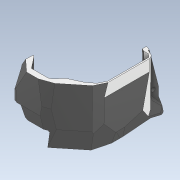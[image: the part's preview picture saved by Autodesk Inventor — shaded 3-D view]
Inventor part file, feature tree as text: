
AUTODESK INVENTOR PART (.ipt)
format: ipt  version: 2022.1 (Build 261234020, 234B)  size: 1,708,032 bytes
history: native  units: mm
features: delete_face x46, move_body x22, chamfer x20, direct_edit x18, sketch x9, projected_geometry x9, extrude x8, plane x4, hole x1, other x1
ambient origin geometry x8: Origin, YZ Plane, XZ Plane, XY Plane, X Axis, Y Axis, Z Axis, Center Point
bodies: Volumenkörper1 (feature_tree)
feature tree (138):
  extrude  "Extrusion1"  Depth=2.0mm TaperAngle=0.0deg
  delete_face  "Fläche löschen1"
  delete_face  "Fläche löschen2"
  delete_face  "Fläche löschen3"
  delete_face  "Fläche löschen4"
  direct_edit  "Direktbearbeitung1"
  plane  "Arbeitsebene2"
  extrude  "Extrusion2"  Depth=1.0mm TaperAngle=0.0deg
  delete_face  "Fläche löschen5"
  delete_face  "Fläche löschen6"
  delete_face  "Fläche löschen7"
  delete_face  "Fläche löschen8"
  delete_face  "Fläche löschen9"
  delete_face  "Fläche löschen10"
  direct_edit  "Direktbearbeitung2"
  delete_face  "Fläche löschen11"
  direct_edit  "Direktbearbeitung3"
  chamfer  "Fase1"  [1 undecoded]
  direct_edit  "Direktbearbeitung4"
  chamfer  "Fase2"  [1 undecoded]
  chamfer  "Fase3"  [1 undecoded]
  delete_face  "Fläche löschen12"
  direct_edit  "Direktbearbeitung5"
  direct_edit  "Direktbearbeitung6"
  direct_edit  "Direktbearbeitung7"
  direct_edit  "Direktbearbeitung8"
  extrude  "Extrusion3"  TaperAngle=0.0deg  [1 undecoded]
  chamfer  "Fase4"  [1 undecoded]
  delete_face  "Fläche löschen13"
  direct_edit  "Direktbearbeitung9"
  delete_face  "Fläche löschen14"
  direct_edit  "Direktbearbeitung10"
  chamfer  "Fase5"  Distance=1.0mm Angle=45.0deg
  direct_edit  "Direktbearbeitung11"
  delete_face  "Fläche löschen15"
  delete_face  "Fläche löschen16"
  chamfer  "Fase6"  Distance=1.598mm Angle=45.0deg
  extrude  "Extrusion4"  TaperAngle=0.0deg  [1 undecoded]
  chamfer  "Fase7"  [1 undecoded]
  delete_face  "Fläche löschen17"
  delete_face  "Fläche löschen18"
  delete_face  "Fläche löschen19"
  delete_face  "Fläche löschen20"
  delete_face  "Fläche löschen21"
  delete_face  "Fläche löschen22"
  delete_face  "Fläche löschen23"
  extrude  "Extrusion5"  Depth=10.0mm TaperAngle=0.0deg
  delete_face  "Fläche löschen24"
  chamfer  "Fase8"  Distance=0.2mm Angle=45.0deg
  delete_face  "Fläche löschen25"
  delete_face  "Fläche löschen26"
  plane  "Arbeitsebene3"
  extrude  "Extrusion6"  TaperAngle=0.0deg  [1 undecoded]
  delete_face  "Fläche löschen27"
  chamfer  "Fase9"  Distance=2.0mm Angle=45.0deg
  direct_edit  "Direktbearbeitung12"
  chamfer  "Fase10"  [1 undecoded]
  chamfer  "Fase11"  [1 undecoded]
  chamfer  "Fase12"  Distance=2.0mm Angle=45.0deg
  chamfer  "Fase13"  Distance=0.6mm
  delete_face  "Fläche löschen28"
  direct_edit  "Direktbearbeitung13"
  delete_face  "Fläche löschen29"
  delete_face  "Fläche löschen30"
  delete_face  "Fläche löschen31"
  delete_face  "Fläche löschen32"
  delete_face  "Fläche löschen33"
  delete_face  "Fläche löschen34"
  chamfer  "Fase14"  Distance=2.0mm Angle=45.0deg
  delete_face  "Fläche löschen35"
  delete_face  "Fläche löschen36"
  direct_edit  "Direktbearbeitung14"
  direct_edit  "Direktbearbeitung15"
  extrude  "Extrusion7"  Depth=1.0mm
  chamfer  "Fase15"  [1 undecoded]
  chamfer  "Fase16"  Distance=1.0mm
  chamfer  "Fase17"  [1 undecoded]
  delete_face  "Fläche löschen37"
  chamfer  "Fase18"  Distance=4.0mm
  delete_face  "Fläche löschen38"
  delete_face  "Fläche löschen39"
  delete_face  "Fläche löschen40"
  delete_face  "Fläche löschen41"
  delete_face  "Fläche löschen42"
  plane  "Arbeitsebene4"
  extrude  "Extrusion8"  Depth=8.0mm
  delete_face  "Fläche löschen43"
  delete_face  "Fläche löschen44"
  chamfer  "Fase19"  Distance=6.0mm
  direct_edit  "Direktbearbeitung16"
  chamfer  "Fase20"  [1 undecoded]
  delete_face  "Fläche löschen45"
  delete_face  "Fläche löschen46"
  direct_edit  "Direktbearbeitung17"
  direct_edit  "Direktbearbeitung18"
  hole  "Bohrung1"  [1 undecoded]
  sketch  "Skizze1"  dims[d0=3.238mm d1=0.0mm d2=0.0mm d3=0.0mm d4=2.0mm]
  projected_geometry  "Projizierte Kontur1"
  plane  "Arbeitsebene1"
  sketch  "Skizze2"  dims[d5=34.906585mm d6=-1.0mm d7=1.0mm d8=0.0mm d9=0.0mm d10=0.0mm d11=-0.4mm d12=0.0mm d13=0.0mm d14=-4.438mm d15=0.0mm d16=0.0mm d17=-2.0mm]
  projected_geometry  "Projizierte Kontur2"
  sketch  "Skizze3"  dims[d18=2.0mm d19=2.0mm d20=45.0deg d21=0.0mm d22=0.0mm d23=-0.5mm d24=0.0mm d25=0.0mm d26=-1.2mm d27=1.0mm d28=2.0mm d29=45.0deg d30=1.598mm d31=2.0mm d32=45.0deg]
  projected_geometry  "Projizierte Kontur3"
  sketch  "Skizze4"  dims[d33=0.0mm d34=-2.5mm d35=0.0mm d36=0.0mm d37=0.0mm d38=-2.0mm d39=0.0mm d40=0.0mm d41=-0.5mm]
  projected_geometry  "Projizierte Kontur4"
  sketch  "Skizze5"  dims[d42=0.0mm d43=0.0mm d44=-0.5mm d47=10.0mm d48=0.0mm d49=0.2mm d50=2.0mm d51=45.0deg]
  projected_geometry  "Projizierte Kontur5"
  projected_geometry  "Projizierte Kontur6"
  sketch  "Skizze6"  dims[d52=0.0mm d53=0.0mm d54=-0.5mm d55=0.0mm d56=0.0mm d57=-0.75mm d58=2.0mm d59=2.0mm d60=45.0deg d61=0.0mm d62=0.0mm d63=-0.5mm d64=0.0mm d65=0.0mm d66=-1.0mm d67=2.0mm d68=2.0mm d69=45.0deg d70=0.6mm d71=0.0mm d72=2.0mm d73=2.0mm d74=45.0deg]
  projected_geometry  "Projizierte Kontur7"
  sketch  "Skizze7"  dims[d75=0.6mm d76=0.0mm d77=1.0mm d78=2.0mm d79=28.553587mm]
  projected_geometry  "Projizierte Kontur8"
  sketch  "Skizze8"  dims[d80=-1.0mm d81=0.0mm d82=0.0mm d83=1.0mm d84=2.0mm d85=28.553587mm d86=0.0mm d87=0.0mm d88=-1.25mm d89=4.0mm d90=2.0mm d91=28.553587mm]
  projected_geometry  "Projizierte Kontur9"
  sketch  "Skizze9"  dims[d92=3.8mm d93=2.0mm d94=28.553587mm d95=5.4mm d96=2.0mm d97=28.553587mm d98=6.0mm d99=2.0mm d100=28.553587mm d101=0.0mm d102=0.0mm d103=-18.0mm d104=3.0mm d105=2.0mm d106=28.553587mm d107=0.0mm d108=0.0mm d109=-0.5mm d110=0.0mm d111=0.0mm d112=1.25mm d113=1.0mm d114=0.0mm d115=1.0mm d116=2.0mm d117=28.553587mm d118=1.0mm d119=2.0mm d120=28.553587mm d121=1.0mm d122=2.0mm d123=28.553587mm d124=1.0mm d125=2.0mm d126=28.553587mm d127=-1.0mm d128=1.0mm d129=0.0mm d130=2.6mm d131=2.0mm d132=28.553587mm d133=0.0mm d134=0.0mm d135=-0.5mm d136=0.0mm d137=0.0mm d138=-0.5mm d139=1.0mm d140=2.0mm d141=28.553587mm d142=0.0mm d143=0.0mm d144=-0.4mm d145=0.0mm d146=0.0mm d147=-0.2mm d148=2.9mm d149=6.0mm d150=4.0mm d151=2.0mm d152=90.0deg d153=8.0mm d154=0.0mm]
  other  "cable_cover_for_pcb"
  move_body  "Verschieben1"
  move_body  "Verschieben2"
  move_body  "Verschieben3"
  move_body  "Verschieben4"
  move_body  "Verschieben5"
  move_body  "Verschieben6"
  move_body  "Verschieben7"
  move_body  "Verschieben8"
  move_body  "Verschieben9"
  move_body  "Verschieben10"
  move_body  "Verschieben11"
  move_body  "Verschieben12"
  move_body  "Verschieben13"
  move_body  "Verschieben14"
  move_body  "Verschieben15"
  move_body  "Verschieben16"
  move_body  "Verschieben17"
  move_body  "Verschieben18"
  move_body  "Verschieben19"
  move_body  "Verschieben20"
  move_body  "Verschieben21"
  move_body  "Verschieben22"
note: 14 required parameter values undecoded (feature->parameter linkage not recoverable at this tier; creation-order binding heuristic only, values carry confidence <= 0.55)
